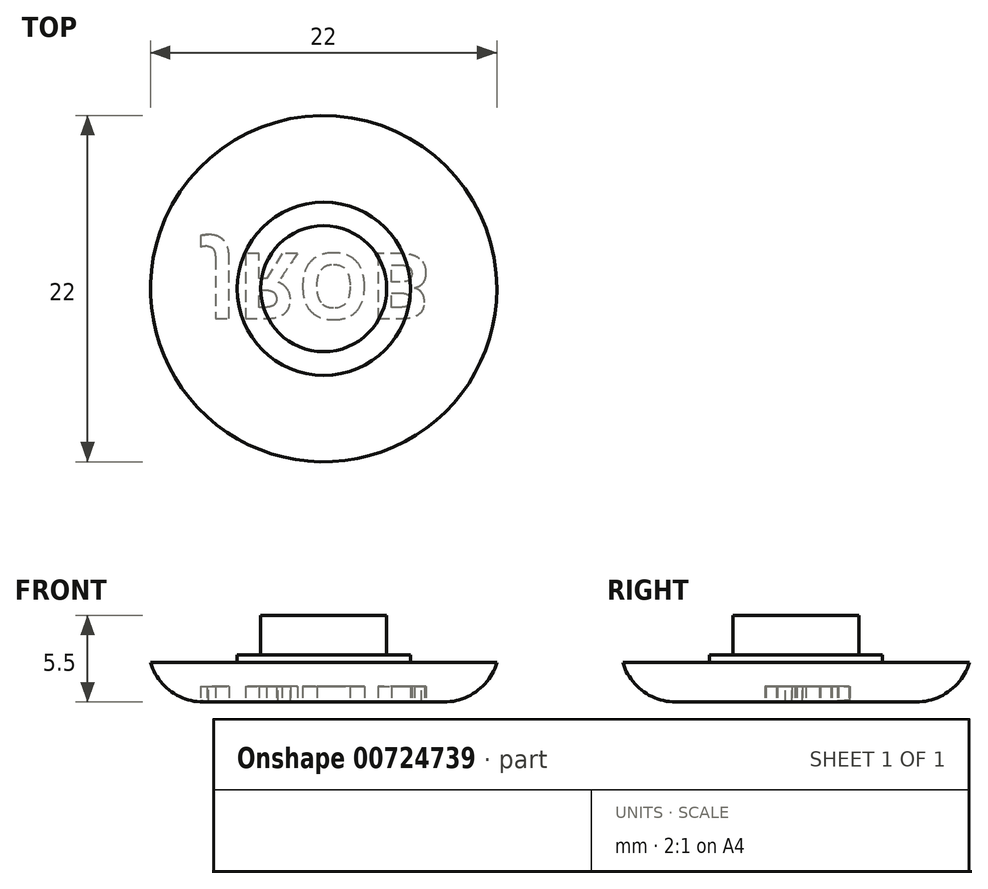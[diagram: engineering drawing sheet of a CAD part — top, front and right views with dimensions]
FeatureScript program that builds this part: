
annotation { "Feature Type Name" : "Feature", "Feature Type Description" : "" }
export const myFeature = defineFeature(function(context is Context, id is Id, definition is map)
    precondition{}
    {
        {
            var Q0;
            Q0=qCreatedBy(makeId("Top.planeOp"),FACE);
            var sketch = newSketch(context, id + "F0", { "sketchPlane" : qUnion([Q0])});
            skCircle(sketch, "E0", {"center": v(0, 0) * mm, "radius": 11 * mm});
            skCircle(sketch, "E1", {"center": v(0, 0) * mm, "radius": 4 * mm});
            skCircle(sketch, "E2", {"center": v(0, 0) * mm, "radius": 5.5 * mm});
            skSolve(sketch);
        }
        {
            var Q0;
            Q0=makeQuery(id+"F0.imprint","IMPRINT",FACE,{"disambiguationData":[TD([[makeQuery(id+"F0.imprint","IMPRINT",EDGE,{"derivedFrom":sQuery(id+"F0.wireOp",EDGE,"E0")}),1.0]])]});
            extrude(context, id + "F1", {"entities" : qUnion([Q0]), "depth" : 2.5 * mm, "offsetDistance" : 25 * mm});
        }
        {
            var Q0;
            Q0=makeQuery(id+"F0.imprint","IMPRINT",FACE,{"disambiguationData":[TD([[makeQuery(id+"F0.imprint","IMPRINT",EDGE,{"derivedFrom":sQuery(id+"F0.wireOp",EDGE,"E1")}),-1.0]])]});
            var Q1;
            Q1=makeQuery(id+"F1.opExtrude","CAP_FACE",FACE,{"disambiguationData":[OSD([sQuery(id+"F0.wireOp",EDGE,"E0"),sQuery(id+"F0.wireOp",EDGE,"E2")])],"isStart":false});
            extrude(context, id + "F2", {"entities" : qUnion([Q0]), "operationType" : NewBodyOperationType.ADD, "endBound" : BoundingType.UP_TO_SURFACE, "depth" : 25 * mm, "endBoundEntityFace" : qUnion([Q1]), "hasOffset" : true, "offsetDistance" : .5 * mm, "offsetOppositeDirection" : true});
        }
        {
            var Q0;
            Q0=makeQuery(id+"F0.imprint","IMPRINT",FACE,{"disambiguationData":[TD([[makeQuery(id+"F0.imprint","IMPRINT",EDGE,{"derivedFrom":sQuery(id+"F0.wireOp",EDGE,"E1")}),1.0]])]});
            var Q1;
            Q1=makeQuery(id+"F2.opExtrude","CAP_FACE",FACE,{"disambiguationData":[OSD([sQuery(id+"F0.wireOp",EDGE,"E0"),sQuery(id+"F0.wireOp",EDGE,"E2")])],"isStart":false});
            extrude(context, id + "F3", {"entities" : qUnion([Q0]), "operationType" : NewBodyOperationType.ADD, "endBound" : BoundingType.UP_TO_SURFACE, "depth" : 3 * mm, "endBoundEntityFace" : qUnion([Q1]), "hasOffset" : true, "offsetDistance" : 2.5 * mm, "offsetOppositeDirection" : true});
        }
        {
            var Q0;
            {var subQ0=sQuery(id+"F0.wireOp",EDGE,"E1");var subQ1=sQuery(id+"F0.wireOp",EDGE,"E2");Q0=makeQuery(id+"F3.boolean.opBoolean","MERGE",FACE,{"derivedFrom":[makeQuery(id+"F2.boolean.opBoolean","MERGE",FACE,{"derivedFrom":[makeQuery(id+"F1.opExtrude","CAP_FACE",FACE,{"disambiguationData":[OSD([sQuery(id+"F0.wireOp",EDGE,"E0"),subQ1])],"isStart":true}),makeQuery(id+"F2.opExtrude","CAP_FACE",FACE,{"disambiguationData":[OSD([subQ0,subQ1])],"isStart":true})]}),makeQuery(id+"F3.opExtrude","CAP_FACE",FACE,{"disambiguationData":[OSD([subQ0])],"isStart":true})]});}
            fillet(context, id + "F4", {"entities" : qUnion([Q0]), "radius" : 3.5 * mm, "tangentPropagation" : true, "allowEdgeOverflow" : false});
        }
        {
            var Q0;
            Q0=qCreatedBy(makeId("Right.planeOp"),FACE);
            var sketch = newSketch(context, id + "F5", { "sketchPlane" : qUnion([Q0])});
            skEllipse(sketch, "E3", {"center": v(-63.43, -1.89) * mm, "majorRadius": 11 * mm, "minorRadius": 2.5 * mm, "majorAxis": v(-1, 0)});
            skPoint(sketch, "E4", {"position": v(-63.43, 0.61) * mm});
            skLineSegment(sketch, "E5", {"start": v(-55.79, 0) * mm, "end": v(-71.08, 0) * mm});
            skArc(sketch, "E6", {"start": v(4.15, 3.3) * mm, "mid": v(11.14, 3.63) * mm, "end": v(4.15, 3.44) * mm});
            skArc(sketch, "E7", {"start": v(-11.15, 3.45) * mm, "mid": v(-11.14, 3.38) * mm, "end": v(-11.14, 3.3) * mm});
            skLineSegment(sketch, "E8", {"start": v(-63.43, 0.61) * mm, "end": v(-63.43, -4.39) * mm});
            skPoint(sketch, "E9.orphan", {"position": v(-63.43, -3.78) * mm});
            skPoint(sketch, "E10.orphan", {"position": v(-63.43, 0) * mm});
            skSolve(sketch);
        }
        {
            var Q0;
            {var subQ0=sQuery(id+"F0.wireOp",EDGE,"E1");var subQ1=sQuery(id+"F0.wireOp",EDGE,"E2");Q0=makeQuery(id+"F3.boolean.opBoolean","MERGE",FACE,{"derivedFrom":[makeQuery(id+"F2.boolean.opBoolean","MERGE",FACE,{"derivedFrom":[makeQuery(id+"F1.opExtrude","CAP_FACE",FACE,{"disambiguationData":[OSD([sQuery(id+"F0.wireOp",EDGE,"E0"),subQ1])],"isStart":true}),makeQuery(id+"F2.opExtrude","CAP_FACE",FACE,{"disambiguationData":[OSD([subQ0,subQ1])],"isStart":true})]}),makeQuery(id+"F3.opExtrude","CAP_FACE",FACE,{"disambiguationData":[OSD([subQ0])],"isStart":true})]});}
            var sketch = newSketch(context, id + "F6", { "sketchPlane" : qUnion([Q0])});
            skText(sketch, "E11", { "text": "JROB", "fontName": "OpenSans-Bold.ttf"});
            const initialGuessF6  = {"E11": [-0.0074, -0.00222, 1, 0, 0.00416]};
            skSetInitialGuess(sketch, initialGuessF6);
            skSolve(sketch);
        }
        {
            var Q0;
            Q0 = qSketchRegion(id + "F6", true);
            extrude(context, id + "F7", {"entities" : qUnion([Q0]), "operationType" : NewBodyOperationType.REMOVE, "oppositeDirection" : true, "depth" : 1 * mm, "offsetDistance" : 25 * mm});
        }
    });
